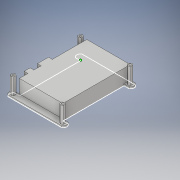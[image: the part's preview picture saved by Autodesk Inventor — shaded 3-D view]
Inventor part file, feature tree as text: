
AUTODESK INVENTOR PART (.ipt)
format: ipt  version: 2019 (Build 230136000, 136)  size: 1,350,144 bytes
history: native  units: mm
features: sketch x7, extrude x5, other x1
ambient origin geometry x8: Origin, YZ Plane, XZ Plane, XY Plane, X Axis, Y Axis, Z Axis, Center Point
bodies: Solid1 (feature_tree)
feature tree (13):
  extrude  "Extrusion1"  Depth=98.58mm
  extrude  "Extrusion2"  Depth=90.0mm
  extrude  "Extrusion3"  Depth=3.0mm
  extrude  "Extrusion4"  Depth=3.0mm
  sketch  "Sketch6"  dims[d8=76.54mm d9=98.58mm]
  extrude  "Extrusion5"  Depth=98.58mm
  sketch  "Sketch8"  dims[d11=81.43mm d12=7.0mm d13=7.0mm d14=2.0mm d15=0.0mm d16=58.04mm d17=98.58mm d18=90.0mm d19=18.0mm d20=0.0mm d21=46.0mm d22=15.0mm d23=20.0mm d24=15.0mm d25=20.0mm d26=8.0mm d27=8.0mm d28=20.0mm d29=5.0mm d30=0.0mm d31=3.0mm d32=3.0mm d33=3.0mm d34=3.0mm d35=5.0mm d36=5.0mm d37=5.0mm d38=5.0mm d39=22.0mm d40=0.0mm d41=27.0mm d42=52.0mm d43=16.0mm d44=2.0mm d45=0.0mm]
  sketch  "Sketch1"  dims[d0=58.04mm d1=98.58mm]
  sketch  "Sketch2"  dims[d2=66.0mm d3=90.0mm]
  sketch  "Sketch3"  dims[d4=3.0mm d5=3.0mm]
  sketch  "Sketch5"  dims[d6=3.0mm d7=3.0mm]
  sketch  "Sketch7"  dims[d10=76.54mm]
  other  "Image1"
